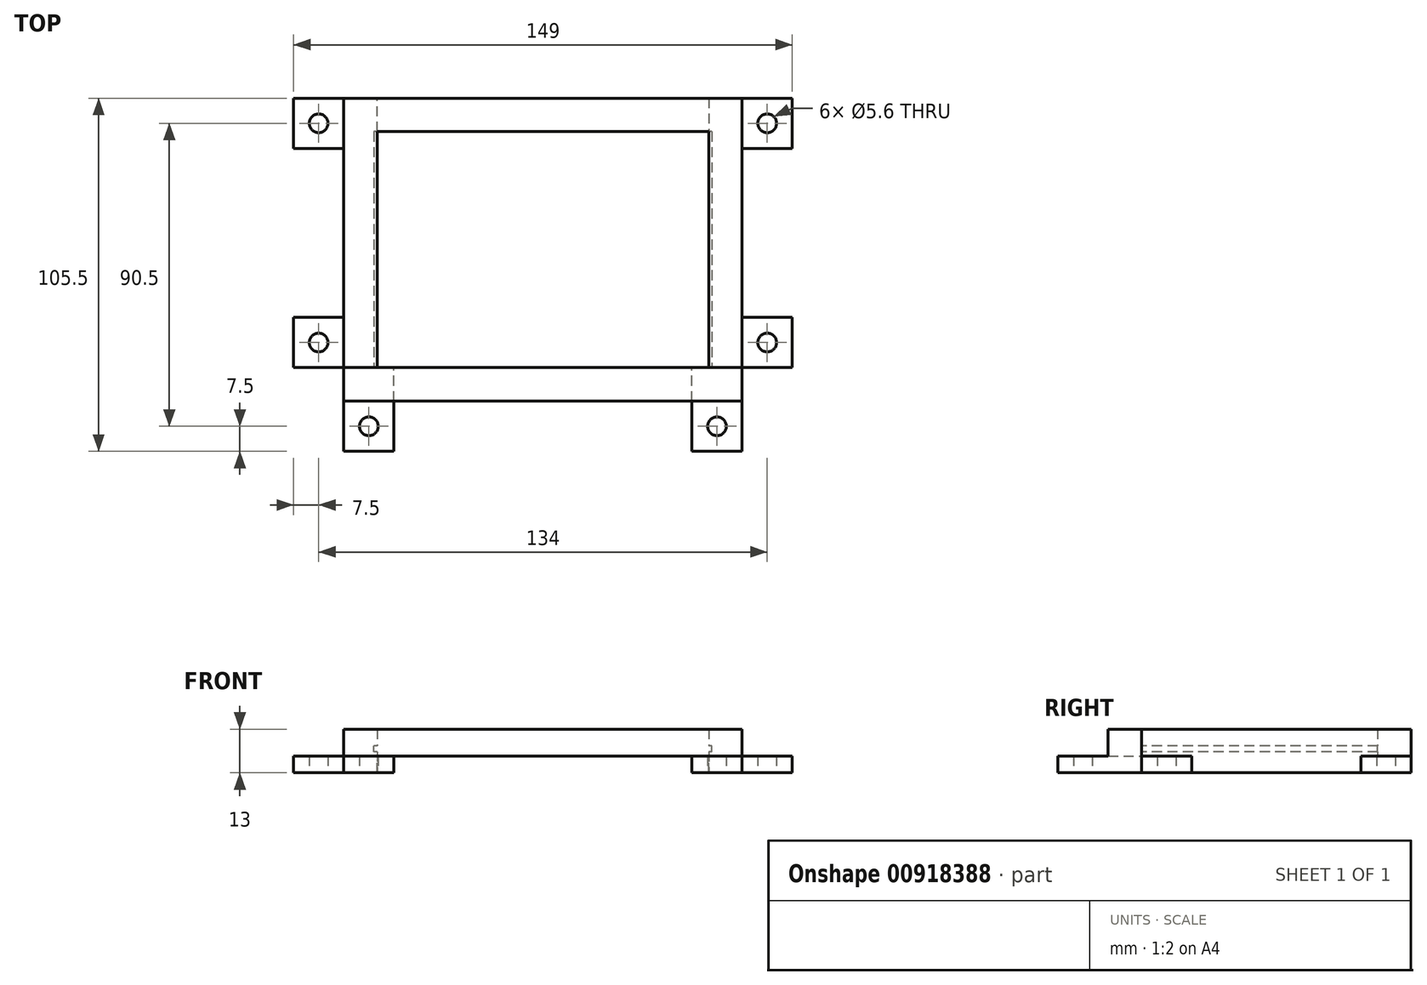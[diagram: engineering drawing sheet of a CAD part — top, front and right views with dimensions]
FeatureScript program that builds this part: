
annotation { "Feature Type Name" : "Feature", "Feature Type Description" : "" }
export const myFeature = defineFeature(function(context is Context, id is Id, definition is map)
    precondition{}
    {
        {
            var Q0;
            Q0=qCreatedBy(makeId("Top.planeOp"),FACE);
            var sketch = newSketch(context, id + "F0", { "sketchPlane" : qUnion([Q0])});
            skLineSegment(sketch, "E0.bottom", {"start": v(49.5, 35.25) * mm, "end": v(-49.5, 35.25) * mm});
            skLineSegment(sketch, "E0.top", {"start": v(59.5, -35.25) * mm, "end": v(-59.5, -35.25) * mm});
            skLineSegment(sketch, "E0.left", {"start": v(49.5, 35.25) * mm, "end": v(49.5, -35.25) * mm});
            skLineSegment(sketch, "E0.right", {"start": v(-49.5, 35.25) * mm, "end": v(-49.5, -35.25) * mm});
            skPoint(sketch, "E0.middle", {"position": v(0, 0) * mm});
            skLineSegment(sketch, "E1.bottom", {"start": v(59.5, 45.25) * mm, "end": v(-59.5, 45.25) * mm});
            skLineSegment(sketch, "E1.left", {"start": v(59.5, 45.25) * mm, "end": v(59.5, -35.25) * mm});
            skLineSegment(sketch, "E1.right", {"start": v(-59.5, 45.25) * mm, "end": v(-59.5, -35.25) * mm});
            skSolve(sketch);
        }
        {
            var Q0;
            Q0=makeQuery(id+"F0.imprint","IMPRINT",FACE,{"disambiguationData":[TD([[makeQuery(id+"F0.imprint","IMPRINT",EDGE,{"derivedFrom":sQuery(id+"F0.wireOp",EDGE,"E0.bottom")}),-1.0]])]});
            extrude(context, id + "F1", {"entities" : qUnion([Q0]), "depth" : 5 * mm, "offsetDistance" : 25 * mm});
        }
        {
            var Q0;
            Q0=makeQuery(id+"F1.opExtrude","CAP_FACE",FACE,{"disambiguationData":[OSD([sQuery(id+"F0.wireOp",EDGE,"E0.bottom"),sQuery(id+"F0.wireOp",EDGE,"E0.top"),sQuery(id+"F0.wireOp",EDGE,"E0.left"),sQuery(id+"F0.wireOp",EDGE,"E0.right"),sQuery(id+"F0.wireOp",EDGE,"E1.bottom"),sQuery(id+"F0.wireOp",EDGE,"E1.left"),sQuery(id+"F0.wireOp",EDGE,"E1.right")])],"isStart":true});
            extrude(context, id + "F2", {"entities" : qUnion([Q0]), "operationType" : NewBodyOperationType.ADD, "depth" : 3 * mm, "offsetDistance" : 25 * mm});
        }
        {
            var Q0;
            Q0=makeQuery(id+"F2.opExtrude","CAP_FACE",FACE,{"disambiguationData":[OSD([sQuery(id+"F0.wireOp",EDGE,"E0.bottom"),sQuery(id+"F0.wireOp",EDGE,"E0.top"),sQuery(id+"F0.wireOp",EDGE,"E0.left"),sQuery(id+"F0.wireOp",EDGE,"E0.right"),sQuery(id+"F0.wireOp",EDGE,"E1.bottom"),sQuery(id+"F0.wireOp",EDGE,"E1.left"),sQuery(id+"F0.wireOp",EDGE,"E1.right")])],"isStart":false});
            var sketch = newSketch(context, id + "F3", { "sketchPlane" : qUnion([Q0])});
            skLineSegment(sketch, "E2", {"start": v(-49.5, -35.25) * mm, "end": v(-49.5, -45.25) * mm});
            skLineSegment(sketch, "E3", {"start": v(49.5, -35.25) * mm, "end": v(49.5, -45.25) * mm});
            skSolve(sketch);
        }
        {
            var Q0;
            {var subQ4=sQuery(id+"F3.wireOp",EDGE,"E2");Q0=makeQuery(id+"F3.imprint","IMPRINT",FACE,{"disambiguationData":[TD([[makeQuery(id+"F3.imprint","IMPRINT",EDGE,{"derivedFrom":subQ4}),-1.0]])]});}
            var Q1;
            {var subQ4=sQuery(id+"F3.wireOp",EDGE,"E3");Q1=makeQuery(id+"F3.imprint","IMPRINT",FACE,{"disambiguationData":[TD([[makeQuery(id+"F3.imprint","IMPRINT",EDGE,{"derivedFrom":subQ4}),1.0]])]});}
            extrude(context, id + "F4", {"entities" : qUnion([Q0, Q1]), "operationType" : NewBodyOperationType.ADD, "depth" : 5 * mm, "offsetDistance" : 25 * mm});
        }
        {
            var Q0;
            Q0=qCreatedBy(makeId("Top.planeOp"),FACE);
            var sketch = newSketch(context, id + "F5", { "sketchPlane" : qUnion([Q0])});
            skLineSegment(sketch, "E4.bottom", {"start": v(50.5, 35.25) * mm, "end": v(-50.5, 35.25) * mm});
            skLineSegment(sketch, "E4.top", {"start": v(50.5, -35.25) * mm, "end": v(-50.5, -35.25) * mm});
            skLineSegment(sketch, "E4.left", {"start": v(50.5, 35.25) * mm, "end": v(50.5, -35.25) * mm});
            skLineSegment(sketch, "E4.right", {"start": v(-50.5, 35.25) * mm, "end": v(-50.5, -35.25) * mm});
            skPoint(sketch, "E4.middle", {"position": v(0, 0) * mm});
            skSolve(sketch);
        }
        {
            var Q0;
            Q0=makeQuery(id+"F5.imprint","IMPRINT",FACE,{"disambiguationData":[TD([[makeQuery(id+"F5.imprint","IMPRINT",EDGE,{"derivedFrom":sQuery(id+"F5.wireOp",EDGE,"E4.bottom")}),1.0]])]});
            extrude(context, id + "F6", {"entities" : qUnion([Q0]), "operationType" : NewBodyOperationType.REMOVE, "oppositeDirection" : true, "depth" : 1.7 * mm, "offsetDistance" : 25 * mm});
        }
        {
            var Q0;
            Q0=makeQuery(id+"F1.opExtrude","CAP_FACE",FACE,{"disambiguationData":[OSD([sQuery(id+"F0.wireOp",EDGE,"E0.bottom"),sQuery(id+"F0.wireOp",EDGE,"E0.top"),sQuery(id+"F0.wireOp",EDGE,"E0.left"),sQuery(id+"F0.wireOp",EDGE,"E0.right"),sQuery(id+"F0.wireOp",EDGE,"E1.bottom"),sQuery(id+"F0.wireOp",EDGE,"E1.left"),sQuery(id+"F0.wireOp",EDGE,"E1.right")])],"isStart":false});
            var sketch = newSketch(context, id + "F7", { "sketchPlane" : qUnion([Q0])});
            skLineSegment(sketch, "E5.bottom", {"start": v(-59.5, -35.25) * mm, "end": v(59.5, -35.25) * mm});
            skLineSegment(sketch, "E5.top", {"start": v(-59.5, -45.25) * mm, "end": v(59.5, -45.25) * mm});
            skLineSegment(sketch, "E5.left", {"start": v(-59.5, -35.25) * mm, "end": v(-59.5, -45.25) * mm});
            skLineSegment(sketch, "E5.right", {"start": v(59.5, -35.25) * mm, "end": v(59.5, -45.25) * mm});
            skSolve(sketch);
        }
        {
            var Q0;
            Q0=makeQuery(id+"F7.imprint","IMPRINT",FACE,{"disambiguationData":[TD([[makeQuery(id+"F7.imprint","IMPRINT",EDGE,{"derivedFrom":sQuery(id+"F7.wireOp",EDGE,"E5.top")}),1.0]])]});
            var Q1;
            Q1=makeQuery(id+"F4.opExtrude","CAP_FACE",FACE,{"disambiguationData":[OSD([sQuery(id+"F0.wireOp",EDGE,"E0.top"),sQuery(id+"F0.wireOp",EDGE,"E0.left"),sQuery(id+"F0.wireOp",EDGE,"E1.bottom"),sQuery(id+"F0.wireOp",EDGE,"E1.left"),sQuery(id+"F3.wireOp",EDGE,"E3")])],"isStart":false});
            extrude(context, id + "F8", {"entities" : qUnion([Q0]), "endBound" : BoundingType.UP_TO_SURFACE, "oppositeDirection" : true, "depth" : 25 * mm, "endBoundEntityFace" : qUnion([Q1]), "offsetDistance" : 25 * mm});
        }
        {
            var Q0;
            Q0=makeQuery(id+"F4.opExtrude","CAP_FACE",FACE,{"disambiguationData":[OSD([sQuery(id+"F0.wireOp",EDGE,"E0.top"),sQuery(id+"F0.wireOp",EDGE,"E0.right"),sQuery(id+"F0.wireOp",EDGE,"E1.bottom"),sQuery(id+"F0.wireOp",EDGE,"E1.right"),sQuery(id+"F3.wireOp",EDGE,"E2")])],"isStart":false});
            var sketch = newSketch(context, id + "F9", { "sketchPlane" : qUnion([Q0])});
            skLineSegment(sketch, "E6.bottom", {"start": v(-59.5, -45.25) * mm, "end": v(-74.5, -45.25) * mm});
            skLineSegment(sketch, "E6.top", {"start": v(-59.5, -30.25) * mm, "end": v(-74.5, -30.25) * mm});
            skLineSegment(sketch, "E6.left", {"start": v(-59.5, -45.25) * mm, "end": v(-59.5, -30.25) * mm});
            skLineSegment(sketch, "E6.right", {"start": v(-74.5, -45.25) * mm, "end": v(-74.5, -30.25) * mm});
            skCircle(sketch, "E7", {"center": v(-67, -37.75) * mm, "radius": 2.8 * mm});
            skPoint(sketch, "E7.centerSnap0", {"position": v(-67, -45.25) * mm});
            skPoint(sketch, "E7.centerSnap1", {"position": v(-74.5, -37.75) * mm});
            skSolve(sketch);
        }
        {
            var Q0;
            Q0=makeQuery(id+"F9.imprint","IMPRINT",FACE,{"disambiguationData":[TD([[makeQuery(id+"F9.imprint","IMPRINT",EDGE,{"derivedFrom":sQuery(id+"F9.wireOp",EDGE,"E6.bottom")}),-1.0]])]});
            extrude(context, id + "F10", {"entities" : qUnion([Q0]), "oppositeDirection" : true, "depth" : 5 * mm, "offsetDistance" : 25 * mm});
        }
        {
            var Q0;
            Q0=makeQuery(id+"F10.opExtrude","SWEPT_BODY",BODY,{"disambiguationData":[OSD([sQuery(id+"F9.wireOp",EDGE,"E6.bottom"),sQuery(id+"F9.wireOp",EDGE,"E6.top"),sQuery(id+"F9.wireOp",EDGE,"E6.left"),sQuery(id+"F9.wireOp",EDGE,"E6.right"),sQuery(id+"F9.wireOp",EDGE,"E7")])]});
            var Q1;
            Q1=makeQuery(id+"F1.opExtrude","CAP_EDGE",EDGE,{"disambiguationData":[OSD([sQuery(id+"F0.wireOp",EDGE,"E1.bottom")])],"isStart":false});
            transform(context, id + "F11", {"entities" : qUnion([Q0]), "transformType" : TransformType.TRANSLATION_ENTITY, "oppositeDirectionEntity" : true, "transformLine" : qUnion([Q1]), "makeCopy" : true});
        }
        {
            var Q0;
            Q0=makeQuery(id+"F11.opPattern","COPY",BODY,{"derivedFrom":makeQuery(id+"F10.opExtrude","SWEPT_BODY",BODY,{"disambiguationData":[OSD([sQuery(id+"F9.wireOp",EDGE,"E6.bottom"),sQuery(id+"F9.wireOp",EDGE,"E6.top"),sQuery(id+"F9.wireOp",EDGE,"E6.left"),sQuery(id+"F9.wireOp",EDGE,"E6.right"),sQuery(id+"F9.wireOp",EDGE,"E7")])]}),"instanceName":"1"});
            var Q1;
            Q1=makeQuery(id+"F10.opExtrude","CAP_EDGE",EDGE,{"disambiguationData":[OSD([sQuery(id+"F9.wireOp",EDGE,"E6.bottom")])],"isStart":false});
            transform(context, id + "F12", {"entities" : qUnion([Q0]), "transformType" : TransformType.TRANSLATION_ENTITY, "oppositeDirectionEntity" : true, "transformLine" : qUnion([Q1]), "makeCopy" : false});
        }
        {
            var Q0;
            Q0=makeQuery(id+"F11.opPattern","COPY",BODY,{"derivedFrom":makeQuery(id+"F10.opExtrude","SWEPT_BODY",BODY,{"disambiguationData":[OSD([sQuery(id+"F9.wireOp",EDGE,"E6.bottom"),sQuery(id+"F9.wireOp",EDGE,"E6.top"),sQuery(id+"F9.wireOp",EDGE,"E6.left"),sQuery(id+"F9.wireOp",EDGE,"E6.right"),sQuery(id+"F9.wireOp",EDGE,"E7")])]}),"instanceName":"1"});
            var Q1;
            Q1=makeQuery(id+"F10.opExtrude","SWEPT_BODY",BODY,{"disambiguationData":[OSD([sQuery(id+"F9.wireOp",EDGE,"E6.bottom"),sQuery(id+"F9.wireOp",EDGE,"E6.top"),sQuery(id+"F9.wireOp",EDGE,"E6.left"),sQuery(id+"F9.wireOp",EDGE,"E6.right"),sQuery(id+"F9.wireOp",EDGE,"E7")])]});
            var Q2;
            Q2=makeQuery(id+"F1.opExtrude","CAP_EDGE",EDGE,{"disambiguationData":[OSD([sQuery(id+"F0.wireOp",EDGE,"E1.right")])],"isStart":false});
            transform(context, id + "F13", {"entities" : qUnion([Q0, Q1]), "transformType" : TransformType.TRANSLATION_ENTITY, "oppositeDirectionEntity" : false, "transformLine" : qUnion([Q2]), "makeCopy" : true});
        }
        {
            var Q0;
            Q0=makeQuery(id+"F13.opPattern","COPY",BODY,{"derivedFrom":makeQuery(id+"F11.opPattern","COPY",BODY,{"derivedFrom":makeQuery(id+"F10.opExtrude","SWEPT_BODY",BODY,{"disambiguationData":[OSD([sQuery(id+"F9.wireOp",EDGE,"E6.bottom"),sQuery(id+"F9.wireOp",EDGE,"E6.top"),sQuery(id+"F9.wireOp",EDGE,"E6.left"),sQuery(id+"F9.wireOp",EDGE,"E6.right"),sQuery(id+"F9.wireOp",EDGE,"E7")])]}),"instanceName":"1"}),"instanceName":"1"});
            var Q1;
            Q1=makeQuery(id+"F13.opPattern","COPY",BODY,{"derivedFrom":makeQuery(id+"F10.opExtrude","SWEPT_BODY",BODY,{"disambiguationData":[OSD([sQuery(id+"F9.wireOp",EDGE,"E6.bottom"),sQuery(id+"F9.wireOp",EDGE,"E6.top"),sQuery(id+"F9.wireOp",EDGE,"E6.left"),sQuery(id+"F9.wireOp",EDGE,"E6.right"),sQuery(id+"F9.wireOp",EDGE,"E7")])]}),"instanceName":"1"});
            var Q2;
            Q2=makeQuery(id+"F13.opPattern","COPY",EDGE,{"derivedFrom":makeQuery(id+"F10.opExtrude","CAP_EDGE",EDGE,{"disambiguationData":[OSD([sQuery(id+"F9.wireOp",EDGE,"E6.right")])],"isStart":false}),"instanceName":"1"});
            transform(context, id + "F14", {"entities" : qUnion([Q0, Q1]), "transformType" : TransformType.TRANSLATION_ENTITY, "oppositeDirectionEntity" : true, "transformLine" : qUnion([Q2]), "makeCopy" : true});
        }
        {
            var Q0;
            Q0=makeQuery(id+"F13.opPattern","COPY",BODY,{"derivedFrom":makeQuery(id+"F11.opPattern","COPY",BODY,{"derivedFrom":makeQuery(id+"F10.opExtrude","SWEPT_BODY",BODY,{"disambiguationData":[OSD([sQuery(id+"F9.wireOp",EDGE,"E6.bottom"),sQuery(id+"F9.wireOp",EDGE,"E6.top"),sQuery(id+"F9.wireOp",EDGE,"E6.left"),sQuery(id+"F9.wireOp",EDGE,"E6.right"),sQuery(id+"F9.wireOp",EDGE,"E7")])]}),"instanceName":"1"}),"instanceName":"1"});
            var Q1;
            Q1=makeQuery(id+"F13.opPattern","COPY",EDGE,{"derivedFrom":makeQuery(id+"F11.opPattern","COPY",EDGE,{"derivedFrom":makeQuery(id+"F10.opExtrude","CAP_EDGE",EDGE,{"disambiguationData":[OSD([sQuery(id+"F9.wireOp",EDGE,"E6.top")])],"isStart":false}),"instanceName":"1"}),"instanceName":"1"});
            transform(context, id + "F15", {"entities" : qUnion([Q0]), "transformType" : TransformType.TRANSLATION_ENTITY, "oppositeDirectionEntity" : false, "transformLine" : qUnion([Q1]), "makeCopy" : false});
        }
        {
            var Q0;
            Q0=makeQuery(id+"F13.opPattern","COPY",BODY,{"derivedFrom":makeQuery(id+"F11.opPattern","COPY",BODY,{"derivedFrom":makeQuery(id+"F10.opExtrude","SWEPT_BODY",BODY,{"disambiguationData":[OSD([sQuery(id+"F9.wireOp",EDGE,"E6.bottom"),sQuery(id+"F9.wireOp",EDGE,"E6.top"),sQuery(id+"F9.wireOp",EDGE,"E6.left"),sQuery(id+"F9.wireOp",EDGE,"E6.right"),sQuery(id+"F9.wireOp",EDGE,"E7")])]}),"instanceName":"1"}),"instanceName":"1"});
            var Q1;
            Q1=makeQuery(id+"F8.opExtrude","CAP_EDGE",EDGE,{"disambiguationData":[OSD([sQuery(id+"F7.wireOp",EDGE,"E5.right")])],"isStart":true});
            transform(context, id + "F16", {"entities" : qUnion([Q0]), "transformType" : TransformType.TRANSLATION_ENTITY, "oppositeDirectionEntity" : false, "transformLine" : qUnion([Q1]), "makeCopy" : false});
        }
        {
            var Q0;
            Q0=makeQuery(id+"F13.opPattern","COPY",BODY,{"derivedFrom":makeQuery(id+"F10.opExtrude","SWEPT_BODY",BODY,{"disambiguationData":[OSD([sQuery(id+"F9.wireOp",EDGE,"E6.bottom"),sQuery(id+"F9.wireOp",EDGE,"E6.top"),sQuery(id+"F9.wireOp",EDGE,"E6.left"),sQuery(id+"F9.wireOp",EDGE,"E6.right"),sQuery(id+"F9.wireOp",EDGE,"E7")])]}),"instanceName":"1"});
            var Q1;
            Q1=makeQuery(id+"F13.opPattern","COPY",EDGE,{"derivedFrom":makeQuery(id+"F10.opExtrude","CAP_EDGE",EDGE,{"disambiguationData":[OSD([sQuery(id+"F9.wireOp",EDGE,"E6.top")])],"isStart":false}),"instanceName":"1"});
            transform(context, id + "F17", {"entities" : qUnion([Q0]), "transformType" : TransformType.TRANSLATION_ENTITY, "oppositeDirectionEntity" : true, "transformLine" : qUnion([Q1]), "makeCopy" : false});
        }
        {
            var Q0;
            Q0=makeQuery(id+"F13.opPattern","COPY",BODY,{"derivedFrom":makeQuery(id+"F10.opExtrude","SWEPT_BODY",BODY,{"disambiguationData":[OSD([sQuery(id+"F9.wireOp",EDGE,"E6.bottom"),sQuery(id+"F9.wireOp",EDGE,"E6.top"),sQuery(id+"F9.wireOp",EDGE,"E6.left"),sQuery(id+"F9.wireOp",EDGE,"E6.right"),sQuery(id+"F9.wireOp",EDGE,"E7")])]}),"instanceName":"1"});
            var Q1;
            Q1=makeQuery(id+"F8.opExtrude","CAP_EDGE",EDGE,{"disambiguationData":[OSD([sQuery(id+"F7.wireOp",EDGE,"E5.left")])],"isStart":true});
            transform(context, id + "F18", {"entities" : qUnion([Q0]), "transformType" : TransformType.TRANSLATION_ENTITY, "oppositeDirectionEntity" : false, "transformLine" : qUnion([Q1]), "makeCopy" : false});
        }
        {
            var Q0;
            Q0=makeQuery(id+"F13.opPattern","COPY",BODY,{"derivedFrom":makeQuery(id+"F11.opPattern","COPY",BODY,{"derivedFrom":makeQuery(id+"F10.opExtrude","SWEPT_BODY",BODY,{"disambiguationData":[OSD([sQuery(id+"F9.wireOp",EDGE,"E6.bottom"),sQuery(id+"F9.wireOp",EDGE,"E6.top"),sQuery(id+"F9.wireOp",EDGE,"E6.left"),sQuery(id+"F9.wireOp",EDGE,"E6.right"),sQuery(id+"F9.wireOp",EDGE,"E7")])]}),"instanceName":"1"}),"instanceName":"1"});
            var Q1;
            Q1=makeQuery(id+"F13.opPattern","COPY",BODY,{"derivedFrom":makeQuery(id+"F10.opExtrude","SWEPT_BODY",BODY,{"disambiguationData":[OSD([sQuery(id+"F9.wireOp",EDGE,"E6.bottom"),sQuery(id+"F9.wireOp",EDGE,"E6.top"),sQuery(id+"F9.wireOp",EDGE,"E6.left"),sQuery(id+"F9.wireOp",EDGE,"E6.right"),sQuery(id+"F9.wireOp",EDGE,"E7")])]}),"instanceName":"1"});
            var Q2;
            Q2=makeQuery(id+"F8.opExtrude","SWEPT_BODY",BODY,{"disambiguationData":[OSD([sQuery(id+"F7.wireOp",EDGE,"E5.bottom"),sQuery(id+"F7.wireOp",EDGE,"E5.top"),sQuery(id+"F7.wireOp",EDGE,"E5.left"),sQuery(id+"F7.wireOp",EDGE,"E5.right")])]});
            booleanBodies(context, id + "F19", {"operationType" : BooleanOperationType.UNION, "tools" : qUnion([Q0, Q1, Q2])});
        }
        {
            var Q0;
            {var subQ0=makeQuery(id+"F10.opExtrude","CAP_FACE",FACE,{"disambiguationData":[OSD([sQuery(id+"F9.wireOp",EDGE,"E6.bottom"),sQuery(id+"F9.wireOp",EDGE,"E6.top"),sQuery(id+"F9.wireOp",EDGE,"E6.left"),sQuery(id+"F9.wireOp",EDGE,"E6.right"),sQuery(id+"F9.wireOp",EDGE,"E7")])],"isStart":true});Q0=makeQuery(id+"F19.opBoolean","MERGE",FACE,{"derivedFrom":[makeQuery(id+"F8.opExtrude","CAP_FACE",FACE,{"disambiguationData":[OSD([sQuery(id+"F7.wireOp",EDGE,"E5.bottom"),sQuery(id+"F7.wireOp",EDGE,"E5.top"),sQuery(id+"F7.wireOp",EDGE,"E5.left"),sQuery(id+"F7.wireOp",EDGE,"E5.right")])],"isStart":false}),makeQuery(id+"F13.opPattern","COPY",FACE,{"derivedFrom":makeQuery(id+"F11.opPattern","COPY",FACE,{"derivedFrom":subQ0,"instanceName":"1"}),"instanceName":"1"}),makeQuery(id+"F13.opPattern","COPY",FACE,{"derivedFrom":subQ0,"instanceName":"1"})]});}
            var sketch = newSketch(context, id + "F20", { "sketchPlane" : qUnion([Q0])});
            skLineSegment(sketch, "E8", {"start": v(-44.5, 45.25) * mm, "end": v(-44.5, 35.25) * mm});
            skLineSegment(sketch, "E9", {"start": v(44.5, 45.25) * mm, "end": v(44.5, 35.25) * mm});
            skSolve(sketch);
        }
        {
            var Q0;
            {var subQ0=sQuery(id+"F20.wireOp",EDGE,"E8");Q0=makeQuery(id+"F20.imprint","IMPRINT",FACE,{"disambiguationData":[TD([[makeQuery(id+"F20.imprint","IMPRINT",EDGE,{"derivedFrom":subQ0}),1.0]])]});}
            var Q1;
            Q1=makeQuery(id+"F2.opExtrude","CAP_FACE",FACE,{"disambiguationData":[OSD([sQuery(id+"F0.wireOp",EDGE,"E0.bottom"),sQuery(id+"F0.wireOp",EDGE,"E0.top"),sQuery(id+"F0.wireOp",EDGE,"E0.left"),sQuery(id+"F0.wireOp",EDGE,"E0.right"),sQuery(id+"F0.wireOp",EDGE,"E1.bottom"),sQuery(id+"F0.wireOp",EDGE,"E1.left"),sQuery(id+"F0.wireOp",EDGE,"E1.right")])],"isStart":false});
            extrude(context, id + "F21", {"entities" : qUnion([Q0]), "operationType" : NewBodyOperationType.REMOVE, "endBound" : BoundingType.UP_TO_SURFACE, "oppositeDirection" : true, "depth" : 25 * mm, "endBoundEntityFace" : qUnion([Q1]), "offsetDistance" : 25 * mm});
        }
    });
